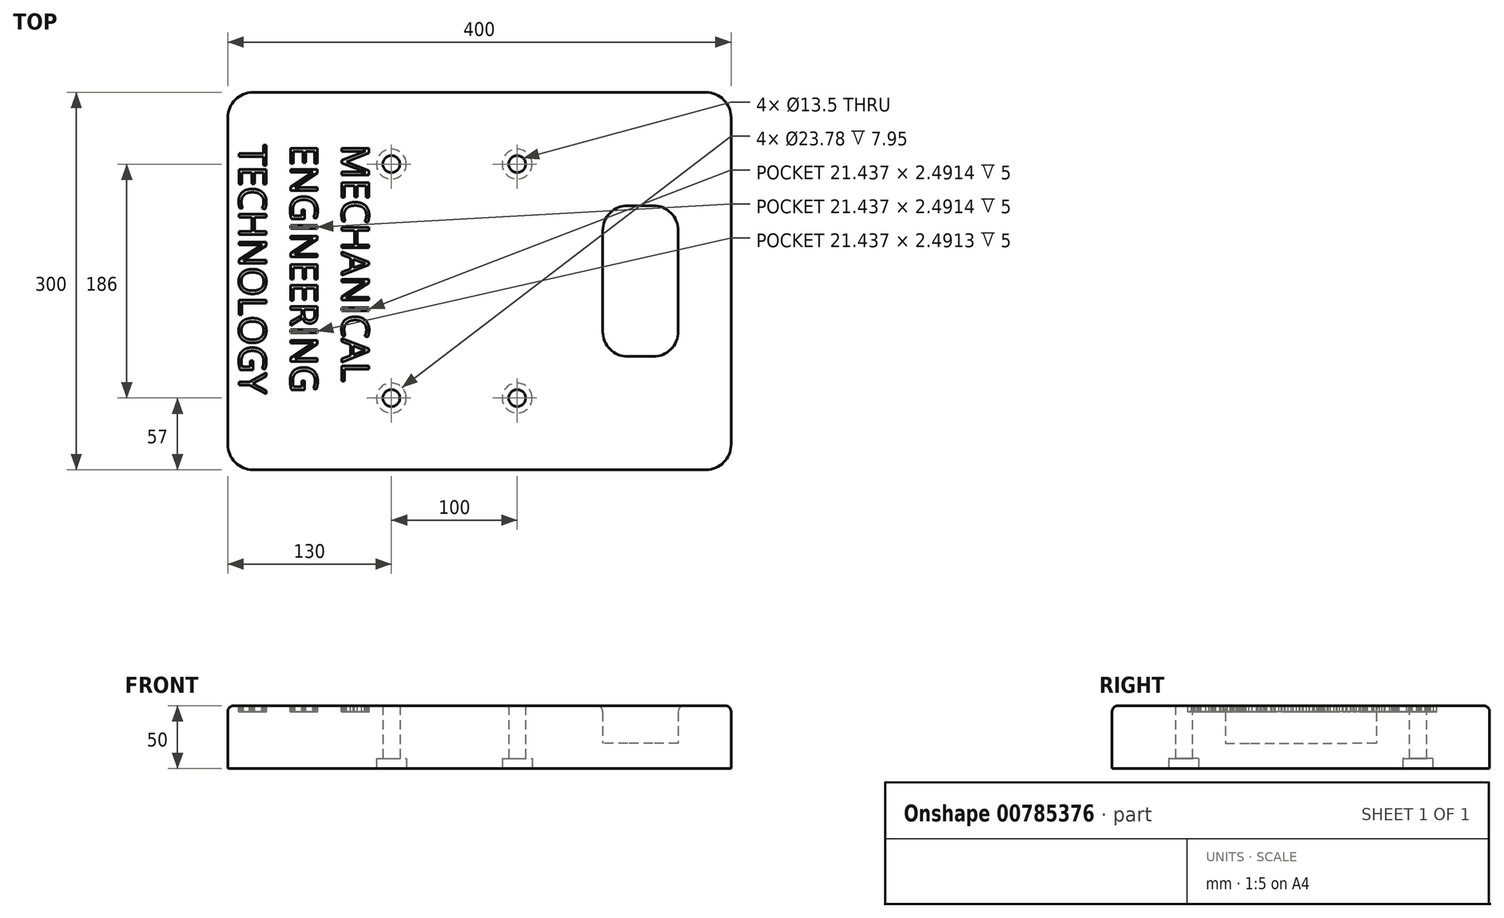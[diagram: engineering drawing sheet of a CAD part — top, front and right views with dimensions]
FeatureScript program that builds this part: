
annotation { "Feature Type Name" : "Feature", "Feature Type Description" : "" }
export const myFeature = defineFeature(function(context is Context, id is Id, definition is map)
    precondition{}
    {
        {
            var Q0;
            Q0=qCreatedBy(makeId("Top.planeOp"),FACE);
            var sketch = newSketch(context, id + "F0", { "sketchPlane" : qUnion([Q0])});
            skLineSegment(sketch, "E0.bottom", {"start": v(180, -150) * mm, "end": v(-180, -150) * mm});
            skLineSegment(sketch, "E0.top", {"start": v(180, 150) * mm, "end": v(-180, 150) * mm});
            skLineSegment(sketch, "E0.left", {"start": v(200, -130) * mm, "end": v(200, 130) * mm});
            skLineSegment(sketch, "E0.right", {"start": v(-200, -130) * mm, "end": v(-200, 130) * mm});
            skPoint(sketch, "E0.middle", {"position": v(0, 0) * mm});
            skLineSegment(sketch, "E1", {"start": v(-200, 0) * mm, "end": v(128, 0) * mm, "construction": true});
            skLineSegment(sketch, "E2.bottom", {"start": v(138, -60) * mm, "end": v(118, -60) * mm});
            skLineSegment(sketch, "E2.top", {"start": v(138, 60) * mm, "end": v(118, 60) * mm});
            skLineSegment(sketch, "E2.left", {"start": v(158, -40) * mm, "end": v(158, 40) * mm});
            skLineSegment(sketch, "E2.right", {"start": v(98, -40) * mm, "end": v(98, 40) * mm});
            skPoint(sketch, "E2.middle", {"position": v(128, 0) * mm});
            skLineSegment(sketch, "E3", {"start": v(200, 0) * mm, "end": v(30, 0) * mm, "construction": true});
            skLineSegment(sketch, "E4", {"start": v(30, 0) * mm, "end": v(30, -93) * mm, "construction": true});
            skLineSegment(sketch, "E5.bottom", {"start": v(30, -93) * mm, "end": v(-70, -93) * mm, "construction": true});
            skLineSegment(sketch, "E5.top", {"start": v(30, 93) * mm, "end": v(-70, 93) * mm, "construction": true});
            skLineSegment(sketch, "E5.left", {"start": v(30, 0) * mm, "end": v(30, 93) * mm, "construction": true});
            skLineSegment(sketch, "E5.right", {"start": v(-70, -93) * mm, "end": v(-70, 93) * mm, "construction": true});
            skPoint(sketch, "E6.visualSharp", {"position": v(158, 60) * mm});
            skArc(sketch, "E6.filletArc", {"start": v(158, 40) * mm, "mid": v(152.14, 54.14) * mm, "end": v(138, 60) * mm});
            skPoint(sketch, "E7.visualSharp", {"position": v(98, 60) * mm});
            skArc(sketch, "E7.filletArc", {"start": v(118, 60) * mm, "mid": v(103.86, 54.14) * mm, "end": v(98, 40) * mm});
            skPoint(sketch, "E8.visualSharp", {"position": v(98, -60) * mm});
            skArc(sketch, "E8.filletArc", {"start": v(98, -40) * mm, "mid": v(103.86, -54.14) * mm, "end": v(118, -60) * mm});
            skPoint(sketch, "E9.visualSharp", {"position": v(158, -60) * mm});
            skArc(sketch, "E9.filletArc", {"start": v(138, -60) * mm, "mid": v(152.14, -54.14) * mm, "end": v(158, -40) * mm});
            skPoint(sketch, "E10.visualSharp", {"position": v(-200, 150) * mm});
            skArc(sketch, "E10.filletArc", {"start": v(-180, 150) * mm, "mid": v(-194.14, 144.14) * mm, "end": v(-200, 130) * mm});
            skPoint(sketch, "E11.visualSharp", {"position": v(200, 150) * mm});
            skArc(sketch, "E11.filletArc", {"start": v(200, 130) * mm, "mid": v(194.14, 144.14) * mm, "end": v(180, 150) * mm});
            skPoint(sketch, "E12.visualSharp", {"position": v(200, -150) * mm});
            skArc(sketch, "E12.filletArc", {"start": v(180, -150) * mm, "mid": v(194.14, -144.14) * mm, "end": v(200, -130) * mm});
            skPoint(sketch, "E13.visualSharp", {"position": v(-200, -150) * mm});
            skArc(sketch, "E13.filletArc", {"start": v(-200, -130) * mm, "mid": v(-194.14, -144.14) * mm, "end": v(-180, -150) * mm});
            skSolve(sketch);
        }
        {
            var Q0;
            Q0=makeQuery(id+"F0.imprint","IMPRINT",FACE,{"disambiguationData":[TD([[makeQuery(id+"F0.imprint","IMPRINT",EDGE,{"derivedFrom":sQuery(id+"F0.wireOp",EDGE,"E0.bottom")}),-1.0]])]});
            extrude(context, id + "F1", {"entities" : qUnion([Q0]), "depth" : 50 * mm});
        }
        {
            var Q0;
            Q0=makeQuery(id+"F0.imprint","IMPRINT",FACE,{"disambiguationData":[TD([[makeQuery(id+"F0.imprint","IMPRINT",EDGE,{"derivedFrom":sQuery(id+"F0.wireOp",EDGE,"E2.bottom")}),-1.0]])]});
            extrude(context, id + "F2", {"entities" : qUnion([Q0]), "operationType" : NewBodyOperationType.ADD, "depth" : 20 * mm});
        }
        {
            var Q0;
            Q0=sQuery(id+"F0.wireOp",VERTEX,"E5.right.start");
            var Q1;
            Q1=sQuery(id+"F0.wireOp",VERTEX,"E5.bottom.start");
            var Q2;
            Q2=sQuery(id+"F0.wireOp",VERTEX,"E5.top.start");
            var Q3;
            Q3=sQuery(id+"F0.wireOp",VERTEX,"E5.top.end");
            var Q4;
            Q4=makeQuery(id+"F1.opExtrude","SWEPT_BODY",BODY,{"disambiguationData":[OSD([sQuery(id+"F0.wireOp",EDGE,"E0.bottom"),sQuery(id+"F0.wireOp",EDGE,"E0.top"),sQuery(id+"F0.wireOp",EDGE,"E0.left"),sQuery(id+"F0.wireOp",EDGE,"E0.right"),sQuery(id+"F0.wireOp",EDGE,"E2.bottom"),sQuery(id+"F0.wireOp",EDGE,"E2.top"),sQuery(id+"F0.wireOp",EDGE,"E2.left"),sQuery(id+"F0.wireOp",EDGE,"E2.right"),sQuery(id+"F0.wireOp",EDGE,"E6.filletArc"),sQuery(id+"F0.wireOp",EDGE,"E7.filletArc"),sQuery(id+"F0.wireOp",EDGE,"E8.filletArc"),sQuery(id+"F0.wireOp",EDGE,"E9.filletArc"),sQuery(id+"F0.wireOp",EDGE,"E10.filletArc"),sQuery(id+"F0.wireOp",EDGE,"E11.filletArc"),sQuery(id+"F0.wireOp",EDGE,"E12.filletArc"),sQuery(id+"F0.wireOp",EDGE,"E13.filletArc")])]});
            hole(context, id + "F3", {"style" : HoleStyle.C_BORE, "endStyle" : HoleEndStyle.THROUGH, "oppositeDirection" : true, "holeDiameter" : 13.5 * mm, "cBoreDiameter" : 23.78 * mm, "cBoreDepth" : 7.95 * mm, "tappedDepth" : 9 * mm, "tapClearance" : 3, "startFromSketch" : true, "locations" : qUnion([Q0, Q1, Q2, Q3]), "scope" : qUnion([Q4])});
        }
        {
            var Q0;
            Q0=makeQuery(id+"F1.opExtrude","CAP_FACE",FACE,{"disambiguationData":[OSD([sQuery(id+"F0.wireOp",EDGE,"E0.bottom"),sQuery(id+"F0.wireOp",EDGE,"E0.top"),sQuery(id+"F0.wireOp",EDGE,"E0.left"),sQuery(id+"F0.wireOp",EDGE,"E0.right"),sQuery(id+"F0.wireOp",EDGE,"E2.bottom"),sQuery(id+"F0.wireOp",EDGE,"E2.top"),sQuery(id+"F0.wireOp",EDGE,"E2.left"),sQuery(id+"F0.wireOp",EDGE,"E2.right"),sQuery(id+"F0.wireOp",EDGE,"E6.filletArc"),sQuery(id+"F0.wireOp",EDGE,"E7.filletArc"),sQuery(id+"F0.wireOp",EDGE,"E8.filletArc"),sQuery(id+"F0.wireOp",EDGE,"E9.filletArc"),sQuery(id+"F0.wireOp",EDGE,"E10.filletArc"),sQuery(id+"F0.wireOp",EDGE,"E11.filletArc"),sQuery(id+"F0.wireOp",EDGE,"E12.filletArc"),sQuery(id+"F0.wireOp",EDGE,"E13.filletArc")])],"isStart":false});
            var sketch = newSketch(context, id + "F4", { "sketchPlane" : qUnion([Q0])});
            skText(sketch, "E14", { "text": "MECHANICAL\nENGINEERING \nTECHNOLOGY", "fontName": "OpenSans-Regular.ttf"});
            const initialGuessF4  = {"E14": [-0.10938, 0.10838, 0, -1, 0.02162]};
            skSetInitialGuess(sketch, initialGuessF4);
            skSolve(sketch);
        }
        {
            var Q0;
            Q0=qSketchRegion(id+"F4",true);
            extrude(context, id + "F5", {"entities" : qUnion([Q0]), "operationType" : NewBodyOperationType.REMOVE, "oppositeDirection" : true, "depth" : 5 * mm});
        }
        {
            var Q0;
            Q0=makeQuery(id+"F1.opExtrude","CAP_EDGE",EDGE,{"disambiguationData":[OSD([sQuery(id+"F0.wireOp",EDGE,"E0.bottom")])],"isStart":false});
            var Q1;
            Q1=makeQuery(id+"F1.opExtrude","CAP_EDGE",EDGE,{"disambiguationData":[OSD([sQuery(id+"F0.wireOp",EDGE,"E2.left")])],"isStart":false});
            var Q2;
            Q2=makeQuery(id+"F2.opExtrude","CAP_EDGE",EDGE,{"disambiguationData":[OSD([sQuery(id+"F0.wireOp",EDGE,"E2.left")])],"isStart":false});
            fillet(context, id + "F6", {"entities" : qUnion([Q0, Q1, Q2]), "radius" : 5 * mm, "tangentPropagation" : true, "allowEdgeOverflow" : false});
        }
    });
